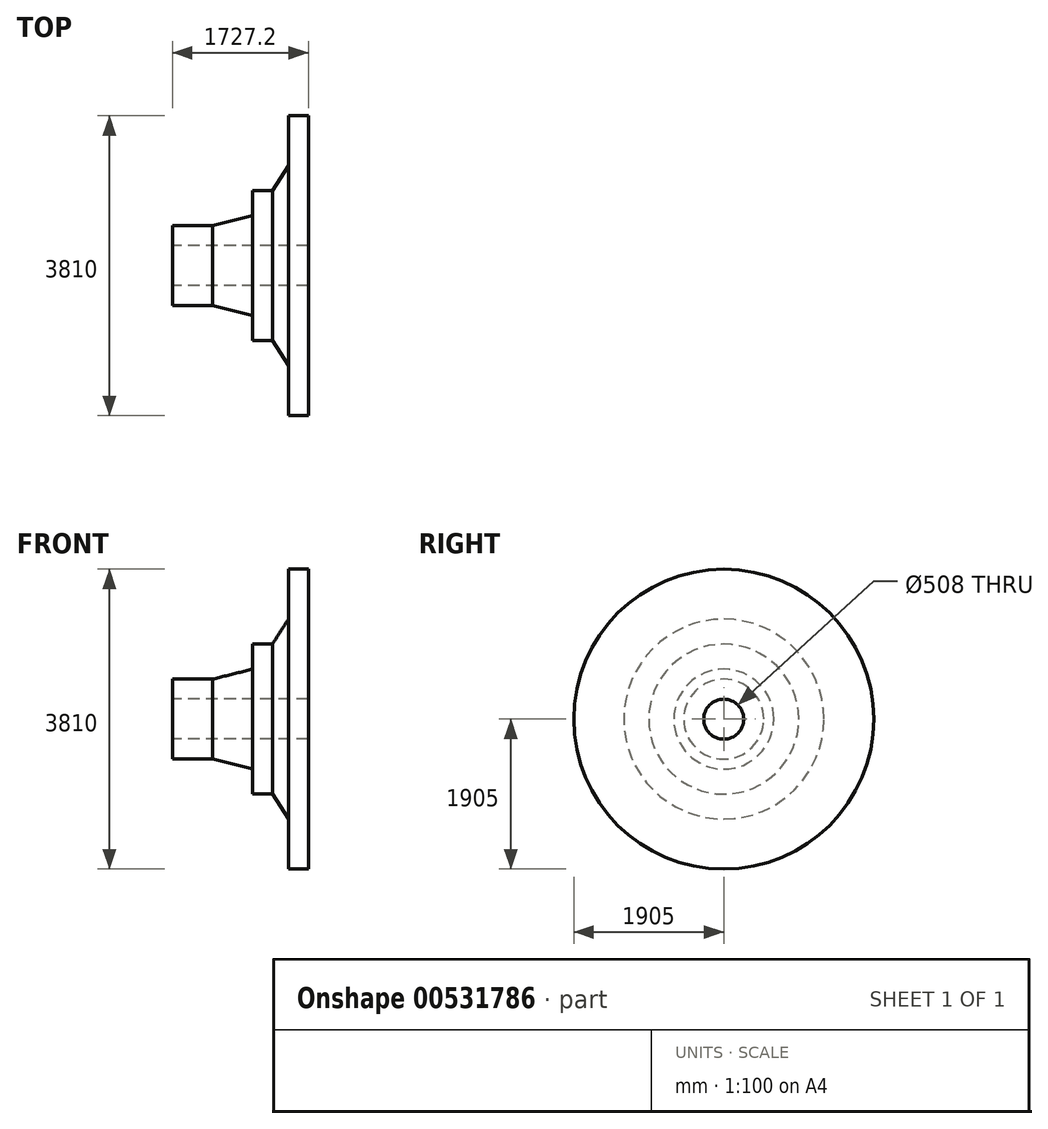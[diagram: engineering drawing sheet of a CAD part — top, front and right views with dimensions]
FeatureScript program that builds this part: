
annotation { "Feature Type Name" : "Feature", "Feature Type Description" : "" }
export const myFeature = defineFeature(function(context is Context, id is Id, definition is map)
    precondition{}
    {
        {
            var Q0;
            Q0=qCreatedBy(makeId("Front.planeOp"),FACE);
            var sketch = newSketch(context, id + "F0", { "sketchPlane" : qUnion([Q0])});
            skLineSegment(sketch, "E0", {"start": v(772.04, 1017.03) * mm, "end": v(518.04, 1017.03) * mm});
            skLineSegment(sketch, "E1", {"start": v(518.04, 1017.03) * mm, "end": v(518.04, 382.03) * mm});
            skLineSegment(sketch, "E2", {"start": v(518.04, 382.03) * mm, "end": v(314.84, 64.53) * mm});
            skLineSegment(sketch, "E3", {"start": v(314.84, 64.53) * mm, "end": v(60.84, 64.53) * mm});
            skLineSegment(sketch, "E4", {"start": v(60.84, 64.53) * mm, "end": v(60.84, -252.97) * mm});
            skLineSegment(sketch, "E5", {"start": v(60.84, -252.97) * mm, "end": v(-447.16, -379.97) * mm});
            skLineSegment(sketch, "E6", {"start": v(-447.16, -379.97) * mm, "end": v(-955.16, -379.97) * mm});
            skLineSegment(sketch, "E7", {"start": v(-955.16, -379.97) * mm, "end": v(-955.16, -633.97) * mm});
            skLineSegment(sketch, "E8", {"start": v(-955.16, -633.97) * mm, "end": v(772.04, -633.97) * mm});
            skLineSegment(sketch, "E9", {"start": v(772.04, -633.97) * mm, "end": v(772.04, 1017.03) * mm});
            skLineSegment(sketch, "E10", {"start": v(-955.16, -887.97) * mm, "end": v(1167.22, -887.97) * mm});
            skSolve(sketch);
        }
        {
            var Q0;
            Q0=makeQuery(id+"F0.imprint","IMPRINT",FACE,{"disambiguationData":[TD([[makeQuery(id+"F0.imprint","IMPRINT",EDGE,{"derivedFrom":sQuery(id+"F0.wireOp",EDGE,"E0")}),1.0]])]});
            var Q1;
            Q1=sQuery(id+"F0.wireOp",EDGE,"E10");
            revolve(context, id + "F1", {"entities" : qUnion([Q0]), "axis" : qUnion([Q1]), "revolveType" : RevolveType.FULL});
        }
    });
